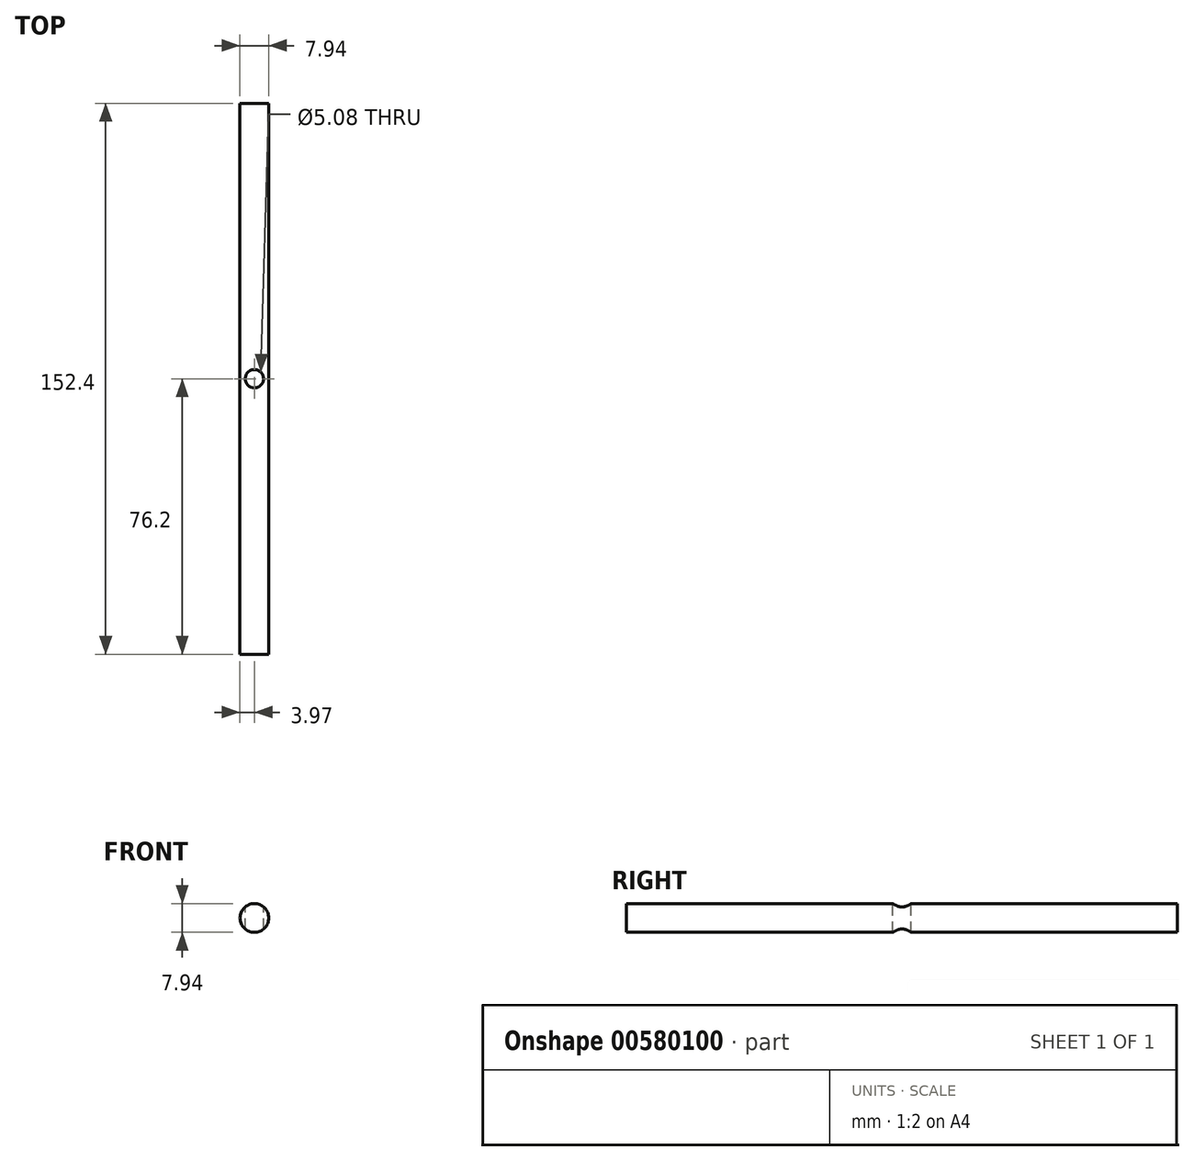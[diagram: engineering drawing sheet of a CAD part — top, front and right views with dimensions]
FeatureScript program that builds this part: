
annotation { "Feature Type Name" : "Feature", "Feature Type Description" : "" }
export const myFeature = defineFeature(function(context is Context, id is Id, definition is map)
    precondition{}
    {
        {
            var Q0;
            Q0=qCreatedBy(makeId("Front.planeOp"),FACE);
            var sketch = newSketch(context, id + "F0", { "sketchPlane" : qUnion([Q0])});
            skCircle(sketch, "E0", {"center": v(0, 0) * mm, "radius": 3.97 * mm});
            skSolve(sketch);
        }
        {
            var Q0;
            Q0=qSketchRegion(id+"F0",true);
            extrude(context, id + "F1", {"entities" : qUnion([Q0]), "depth" : 152.4 * mm, "symmetric" : true});
        }
        {
            var Q0;
            Q0=qCreatedBy(makeId("Top.planeOp"),FACE);
            var sketch = newSketch(context, id + "F2", { "sketchPlane" : qUnion([Q0])});
            skCircle(sketch, "E1", {"center": v(0, 0) * mm, "radius": 2.54 * mm});
            skSolve(sketch);
        }
        {
            var Q0;
            Q0=qSketchRegion(id+"F2",true);
            extrude(context, id + "F3", {"entities" : qUnion([Q0]), "operationType" : NewBodyOperationType.REMOVE, "oppositeDirection" : true, "depth" : 25.4 * mm, "offsetDistance" : 25.4 * mm, "symmetric" : true});
        }
    });
